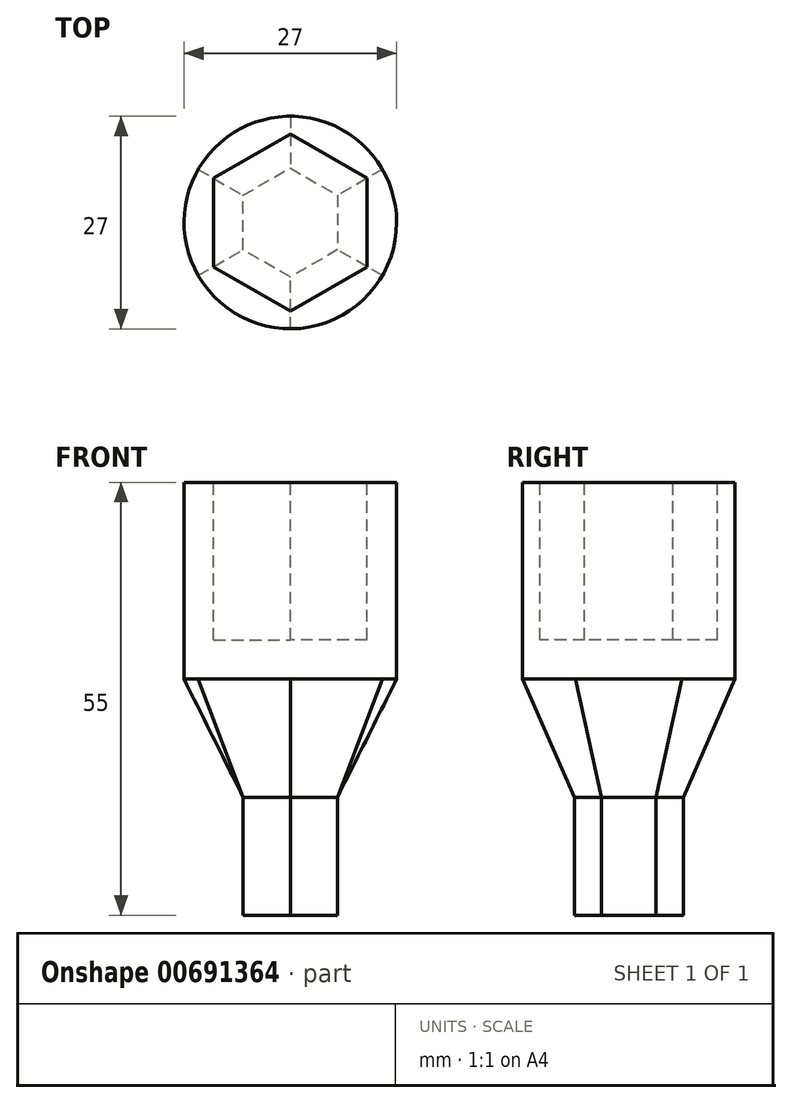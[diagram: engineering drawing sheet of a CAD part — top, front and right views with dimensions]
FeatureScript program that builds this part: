
annotation { "Feature Type Name" : "Feature", "Feature Type Description" : "" }
export const myFeature = defineFeature(function(context is Context, id is Id, definition is map)
    precondition{}
    {
        {
            var Q0;
            Q0=qCreatedBy(makeId("Top.planeOp"),FACE);
            var sketch = newSketch(context, id + "F0", { "sketchPlane" : qUnion([Q0])});
            skCircle(sketch, "E0", {"center": v(0, 0) * mm, "radius": 13.5 * mm});
            skSolve(sketch);
        }
        {
            var Q0;
            Q0 = qSketchRegion(id + "F0", true);
            extrude(context, id + "F1", {"entities" : qUnion([Q0]), "depth" : 25 * mm, "offsetDistance" : 25 * mm});
        }
        {
            var Q0;
            Q0=makeQuery(id+"F1.opExtrude","CAP_FACE",FACE,{"disambiguationData":[OSD([sQuery(id+"F0.wireOp",EDGE,"E0")])],"isStart":false});
            var sketch = newSketch(context, id + "F2", { "sketchPlane" : qUnion([Q0])});
            skCircle(sketch, "E1.cCircle", {"center": v(0, 0) * mm, "radius": 11.26 * mm, "construction": true});
            skLineSegment(sketch, "E1.0", {"start": v(9.75, -5.63) * mm, "end": v(0, -11.26) * mm});
            skLineSegment(sketch, "E1.1", {"start": v(0, -11.26) * mm, "end": v(-9.75, -5.63) * mm});
            skLineSegment(sketch, "E1.2", {"start": v(-9.75, -5.63) * mm, "end": v(-9.75, 5.63) * mm});
            skLineSegment(sketch, "E1.3", {"start": v(-9.75, 5.63) * mm, "end": v(0, 11.26) * mm});
            skLineSegment(sketch, "E1.4", {"start": v(0, 11.26) * mm, "end": v(9.75, 5.63) * mm});
            skLineSegment(sketch, "E1.5", {"start": v(9.75, 5.63) * mm, "end": v(9.75, -5.63) * mm});
            skSolve(sketch);
        }
        {
            var Q0;
            Q0=makeQuery(id+"F2.imprint","IMPRINT",FACE,{"disambiguationData":[TD([[makeQuery(id+"F2.imprint","IMPRINT",EDGE,{"derivedFrom":sQuery(id+"F2.wireOp",EDGE,"E1.0")}),-1.0]])]});
            extrude(context, id + "F3", {"entities" : qUnion([Q0]), "operationType" : NewBodyOperationType.REMOVE, "oppositeDirection" : true, "depth" : 20 * mm, "offsetDistance" : 25 * mm});
        }
        {
            var Q0;
            Q0=qCreatedBy(makeId("Top.planeOp"),FACE);
            cPlane(context, id + "F4", {"entities" : qUnion([Q0]), "cplaneType" : CPlaneType.OFFSET, "offset" : 15 * mm, "oppositeDirection" : true, "width" : 150 * mm, "height" : 150 * mm});
        }
        {
            var Q0;
            Q0=qCreatedBy(id+"F4.planeOp",FACE);
            var sketch = newSketch(context, id + "F5", { "sketchPlane" : qUnion([Q0])});
            skCircle(sketch, "E2.cCircle", {"center": v(0, 0) * mm, "radius": 6.93 * mm, "construction": true});
            skLineSegment(sketch, "E2.0", {"start": v(6, -3.46) * mm, "end": v(0, -6.93) * mm});
            skLineSegment(sketch, "E2.1", {"start": v(0, -6.93) * mm, "end": v(-6, -3.46) * mm});
            skLineSegment(sketch, "E2.2", {"start": v(-6, -3.46) * mm, "end": v(-6, 3.46) * mm});
            skLineSegment(sketch, "E2.3", {"start": v(-6, 3.46) * mm, "end": v(0, 6.93) * mm});
            skLineSegment(sketch, "E2.4", {"start": v(0, 6.93) * mm, "end": v(6, 3.46) * mm});
            skLineSegment(sketch, "E2.5", {"start": v(6, 3.46) * mm, "end": v(6, -3.46) * mm});
            skSolve(sketch);
        }
        {
            var Q1;
            Q1=makeQuery(id+"F1.opExtrude","CAP_FACE",FACE,{"disambiguationData":[OSD([sQuery(id+"F0.wireOp",EDGE,"E0")])],"isStart":true});
            var Q2;
            Q2=makeQuery(id+"F5.imprint","IMPRINT",FACE,{"disambiguationData":[TD([[makeQuery(id+"F5.imprint","IMPRINT",EDGE,{"derivedFrom":sQuery(id+"F5.wireOp",EDGE,"E2.0")}),-1.0]])]});
            loft(context, id + "F6", {"operationType" : NewBodyOperationType.ADD, "sheetProfilesArray" : [{ "sheetProfileEntities" : qUnion([Q1]) }, { "sheetProfileEntities" : qUnion([Q2]) }]});
        }
        {
            var Q0;
            Q0=makeQuery(id+"F6.opLoft","CAP_FACE",FACE,{"disambiguationData":[OSD([makeQuery(id+"F5.imprint","IMPRINT",FACE,{"disambiguationData":[TD([[makeQuery(id+"F5.imprint","IMPRINT",EDGE,{"derivedFrom":sQuery(id+"F5.wireOp",EDGE,"E2.0")}),-1.0]])]})])],"isStart":true});
            extrude(context, id + "F7", {"entities" : qUnion([Q0]), "operationType" : NewBodyOperationType.ADD, "depth" : 15 * mm, "offsetDistance" : 25 * mm});
        }
    });
